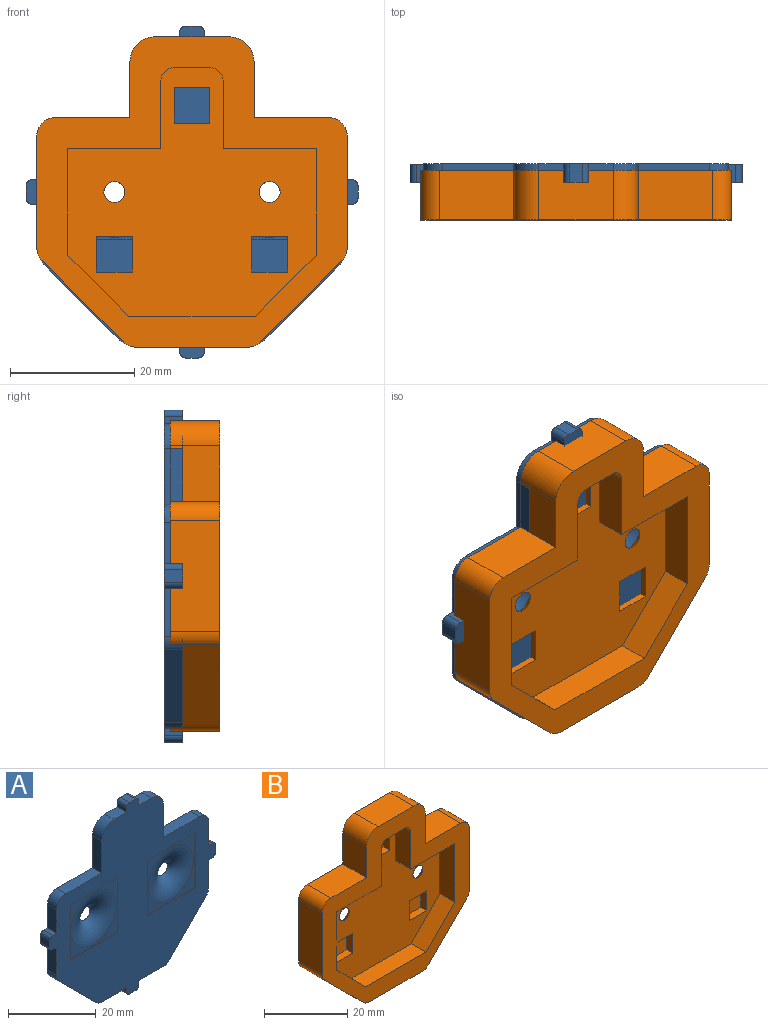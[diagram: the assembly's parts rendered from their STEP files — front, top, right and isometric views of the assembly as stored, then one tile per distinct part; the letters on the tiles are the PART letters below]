
ASSEMBLY  parts=2 mates=1
PART A: 71 faces, bbox 53.5x7.2x53.5 mm
  f0: plane 53.5x53.5mm, normal (0,-1,0), area 1397.6mm2, adj f2,f3,f4,f5,f6,f7,f8,f9
  f1: plane 53.5x53.5mm, normal (0,1,0), area 1752.8mm2, adj f2,f3,f4,f5,f6,f7,f8,f9
  f2: plane 6.55x3mm, normal (-1,0,0), area 19.7mm2, adj f0,f1,f3,f32
  f3: plane 3x1.2mm, normal (0,0,1), area 3.6mm2, adj f0,f1,f2,f69
  f4: plane 3x2mm, normal (-1,0,0), area 6mm2, adj f0,f1,f69,f70
  f5: plane 3x1.2mm, normal (0,0,-1), area 3.6mm2, adj f0,f1,f6,f70
  f6: plane 7.8x3mm, normal (-1,0,0), area 23.4mm2, adj f0,f1,f5,f30
  f7: plane 11.75x11.75mm, normal (-0.71,0,-0.71), area 49.9mm2, adj f0,f1,f30,f31
  f8: plane 7.8x3mm, normal (0,0,-1), area 23.4mm2, adj f0,f1,f9,f31
  f9: plane 3x1.2mm, normal (-1,0,0), area 3.6mm2, adj f0,f1,f8,f67
  f10: plane 3x2mm, normal (0,0,-1), area 6mm2, adj f0,f1,f67,f68
  f11: plane 3x1.2mm, normal (1,0,0), area 3.6mm2, adj f0,f1,f12,f68
  f12: plane 7.8x3mm, normal (0,0,-1), area 23.4mm2, adj f0,f1,f11,f33
  f13: plane 11.75x11.75mm, normal (0.71,0,-0.71), area 49.9mm2, adj f0,f1,f33,f34
  f14: plane 7.8x3mm, normal (1,0,0), area 23.4mm2, adj f0,f1,f15,f34
  f15: plane 3x1.2mm, normal (0,0,-1), area 3.6mm2, adj f0,f1,f14,f65
  f16: plane 3x2mm, normal (1,0,0), area 6mm2, adj f0,f1,f65,f66
  f17: plane 3x1.2mm, normal (0,0,1), area 3.6mm2, adj f0,f1,f18,f66
  f18: plane 6.55x3mm, normal (1,0,0), area 19.7mm2, adj f0,f1,f17,f35
  f19: plane 11.55x3mm, normal (0,0,1), area 34.6mm2, adj f0,f1,f20,f35
  f20: plane 9x3mm, normal (1,0,0), area 27mm2, adj f0,f1,f19,f21
  f21: cylinder r=4mm len=4mm, axis (0,1,0), area 18.8mm2, adj f0,f1,f20,f22
  f22: plane 4x3mm, normal (0,0,1), area 12mm2, adj f0,f1,f21,f23
  f23: plane 3x1.2mm, normal (1,0,0), area 3.6mm2, adj f0,f1,f22,f63
  f24: plane 3x2mm, normal (0,0,1), area 6mm2, adj f0,f1,f63,f64
  f25: plane 3x1.2mm, normal (-1,0,0), area 3.6mm2, adj f0,f1,f26,f64
  f26: plane 4x3mm, normal (0,0,1), area 12mm2, adj f0,f1,f25,f27
  f27: cylinder r=4mm len=4mm, axis (0,1,0), area 18.8mm2, adj f0,f1,f26,f28
  f28: plane 9x3mm, normal (-1,0,0), area 27mm2, adj f0,f1,f27,f29
  f29: plane 11.55x3mm, normal (0,0,1), area 34.6mm2, adj f0,f1,f28,f32
  f30: cylinder r=3mm len=3mm, axis (0,1,0), area 7.1mm2, adj f0,f1,f6,f7
  f31: cylinder r=3mm len=3mm, axis (0,1,0), area 7.1mm2, adj f0,f1,f7,f8
  f32: cylinder r=3mm len=3mm, axis (0,-1,0), area 14.1mm2, adj f0,f1,f2,f29
  f33: cylinder r=3mm len=3mm, axis (0,1,0), area 7.1mm2, adj f0,f1,f12,f13
  f34: cylinder r=3mm len=3mm, axis (0,-1,0), area 7.1mm2, adj f0,f1,f13,f14
  f35: cylinder r=3mm len=3mm, axis (0,1,0), area 14.1mm2, adj f0,f1,f18,f19
  f36: plane 5.8x2mm, normal (0,0,1), area 11.6mm2, adj f1,f37,f39,f40
  f37: plane 5.8x2mm, normal (1,0,0), area 11.6mm2, adj f1,f36,f38,f40
  f38: plane 5.8x2mm, normal (0,0,-1), area 11.6mm2, adj f1,f37,f39,f40
  f39: plane 5.8x2mm, normal (-1,0,0), area 11.6mm2, adj f1,f36,f38,f40
  f40: plane 5.8x5.8mm, normal (0,1,0), area 33.6mm2, adj f36,f37,f38,f39
  f41: plane 5.8x2mm, normal (0,0,1), area 11.6mm2, adj f1,f42,f44,f45
  f42: plane 5.8x2mm, normal (1,0,0), area 11.6mm2, adj f1,f41,f43,f45
  f43: plane 5.8x2mm, normal (0,0,-1), area 11.6mm2, adj f1,f42,f44,f45
  f44: plane 5.8x2mm, normal (-1,0,0), area 11.6mm2, adj f1,f41,f43,f45
  f45: plane 5.8x5.8mm, normal (0,1,0), area 33.6mm2, adj f41,f42,f43,f44
  f46: plane 5.8x2mm, normal (-1,0,0), area 11.6mm2, adj f1,f47,f49,f50
  f47: plane 5.8x2mm, normal (0,0,1), area 11.6mm2, adj f1,f46,f48,f50
  f48: plane 5.8x2mm, normal (1,0,0), area 11.6mm2, adj f1,f47,f49,f50
  f49: plane 5.8x2mm, normal (0,0,-1), area 11.6mm2, adj f1,f46,f48,f50
  f50: plane 5.8x5.8mm, normal (0,1,0), area 33.6mm2, adj f46,f47,f48,f49
  f51: plane 15.4x0.2mm, normal (0,0,-1), area 3.1mm2, adj f0,f52,f54,f55
  f52: plane 15.4x0.2mm, normal (1,0,0), area 3.1mm2, adj f0,f51,f53,f55
  f53: plane 15.4x0.2mm, normal (0,0,1), area 3.1mm2, adj f0,f52,f54,f55
  f54: plane 15.4x0.2mm, normal (-1,0,0), area 3.1mm2, adj f0,f51,f53,f55
  f55: plane 15.4x15.4mm, normal (0,-1,0), area 69.7mm2, adj f51,f52,f53,f54,f61
  f56: plane 15.4x0.2mm, normal (-1,0,0), area 3.1mm2, adj f0,f57,f59,f60
  f57: plane 15.4x0.2mm, normal (0,0,-1), area 3.1mm2, adj f0,f56,f58,f60
  f58: plane 15.4x0.2mm, normal (1,0,0), area 3.1mm2, adj f0,f57,f59,f60
  f59: plane 15.4x0.2mm, normal (0,0,1), area 3.1mm2, adj f0,f56,f58,f60
  f60: plane 15.4x15.4mm, normal (0,-1,0), area 69.7mm2, adj f56,f57,f58,f59,f62
  f61: torus R=7.3mm, axis (0,-1,0), area 174.6mm2, adj f1,f55
  f62: torus R=7.3mm, axis (0,-1,0), area 174.6mm2, adj f1,f60
  f63: cylinder r=1mm len=3mm, axis (0,1,0), area 4.7mm2, adj f0,f1,f23,f24
  f64: cylinder r=1mm len=3mm, axis (0,-1,0), area 4.7mm2, adj f0,f1,f24,f25
  f65: cylinder r=1mm len=3mm, axis (0,-1,0), area 4.7mm2, adj f0,f1,f15,f16
  f66: cylinder r=1mm len=3mm, axis (0,1,0), area 4.7mm2, adj f0,f1,f16,f17
  f67: cylinder r=1mm len=3mm, axis (0,1,0), area 4.7mm2, adj f0,f1,f9,f10
  f68: cylinder r=1mm len=3mm, axis (0,-1,0), area 4.7mm2, adj f0,f1,f10,f11
  f69: cylinder r=1mm len=3mm, axis (0,-1,0), area 4.7mm2, adj f0,f1,f3,f4
  f70: cylinder r=1mm len=3mm, axis (0,1,0), area 4.7mm2, adj f0,f1,f4,f5
PART B: 60 faces, bbox 50x8x50 mm
  f0: plane 40x40mm, normal (0,-1,0), area 993.2mm2, adj f14,f15,f16,f17,f18,f19,f20,f21
  f1: plane 50x50mm, normal (0,1,0), area 1405.1mm2, adj f2,f3,f4,f5,f6,f7,f8,f9
  f2: plane 17.91x8mm, normal (0,0,-1), area 143.3mm2, adj f1,f26,f39,f40
  f3: plane 13.04x13.04mm, normal (0.71,0,-0.71), area 147.6mm2, adj f1,f26,f40,f41
  f4: plane 17.96x8mm, normal (1,0,0), area 143.7mm2, adj f1,f26,f41,f42
  f5: plane 12x8mm, normal (0,0,1), area 96mm2, adj f1,f6,f26,f42
  f6: plane 9x8mm, normal (1,0,0), area 72mm2, adj f1,f5,f7,f26
  f7: cylinder r=4mm len=8mm, axis (0,1,0), area 50.3mm2, adj f1,f6,f8,f26
  f8: plane 12x8mm, normal (0,0,1), area 96mm2, adj f1,f7,f9,f26
  f9: cylinder r=4mm len=8mm, axis (0,1,0), area 50.3mm2, adj f1,f8,f10,f26
  f10: plane 9x8mm, normal (-1,0,0), area 72mm2, adj f1,f9,f11,f26
  f11: plane 12x8mm, normal (0,0,1), area 96mm2, adj f1,f10,f26,f37
  f12: plane 17.96x8mm, normal (-1,0,0), area 143.7mm2, adj f1,f26,f37,f38
  f13: plane 13.04x13.04mm, normal (-0.71,0,-0.71), area 147.6mm2, adj f1,f26,f38,f39
  f14: plane 15x5mm, normal (0,0,-1), area 75mm2, adj f0,f15,f25,f26
  f15: plane 11x5mm, normal (1,0,0), area 55mm2, adj f0,f14,f16,f26
  f16: cylinder r=2mm len=5mm, axis (0,1,0), area 15.7mm2, adj f0,f15,f17,f26
  f17: plane 6x5mm, normal (0,0,-1), area 30mm2, adj f0,f16,f18,f26
  f18: cylinder r=2mm len=5mm, axis (0,1,0), area 15.7mm2, adj f0,f17,f19,f26
  f19: plane 11x5mm, normal (-1,0,0), area 55mm2, adj f0,f18,f20,f26
  f20: plane 15x5mm, normal (0,0,-1), area 75mm2, adj f0,f19,f21,f26
  f21: plane 17.2x5mm, normal (-1,0,0), area 86mm2, adj f0,f20,f22,f26
  f22: plane 9.8x9.8mm, normal (-0.71,0,0.71), area 69.3mm2, adj f0,f21,f23,f26
  f23: plane 20.4x5mm, normal (0,0,1), area 102mm2, adj f0,f22,f24,f26
  f24: plane 9.8x9.8mm, normal (0.71,0,0.71), area 69.3mm2, adj f0,f23,f25,f26
  f25: plane 17.2x5mm, normal (1,0,0), area 86mm2, adj f0,f14,f24,f26
  f26: plane 50x50mm, normal (0,-1,0), area 767.2mm2, adj f2,f3,f4,f5,f6,f7,f8,f9
  f27: plane 15.4x0.2mm, normal (0,0,-1), area 3.1mm2, adj f1,f28,f30,f31
  f28: plane 15.4x0.2mm, normal (-1,0,0), area 3.1mm2, adj f1,f27,f29,f31
  f29: plane 15.4x0.2mm, normal (0,0,1), area 3.1mm2, adj f1,f28,f30,f31
  f30: plane 15.4x0.2mm, normal (1,0,0), area 3.1mm2, adj f1,f27,f29,f31
  f31: plane 15.4x15.4mm, normal (0,1,0), area 69.7mm2, adj f27,f28,f29,f30,f58
  f32: plane 15.4x0.2mm, normal (1,0,0), area 3.1mm2, adj f1,f33,f35,f36
  f33: plane 15.4x0.2mm, normal (0,0,-1), area 3.1mm2, adj f1,f32,f34,f36
  f34: plane 15.4x0.2mm, normal (-1,0,0), area 3.1mm2, adj f1,f33,f35,f36
  f35: plane 15.4x0.2mm, normal (0,0,1), area 3.1mm2, adj f1,f32,f34,f36
  f36: plane 15.4x15.4mm, normal (0,1,0), area 69.7mm2, adj f32,f33,f34,f35,f59
  f37: cylinder r=3mm len=8mm, axis (0,-1,0), area 37.7mm2, adj f1,f11,f12,f26
  f38: cylinder r=3mm len=8mm, axis (0,1,0), area 18.8mm2, adj f1,f12,f13,f26
  f39: cylinder r=3mm len=8mm, axis (0,1,0), area 18.8mm2, adj f1,f2,f13,f26
  f40: cylinder r=3mm len=8mm, axis (0,1,0), area 18.8mm2, adj f1,f2,f3,f26
  f41: cylinder r=3mm len=8mm, axis (0,-1,0), area 18.8mm2, adj f1,f3,f4,f26
  f42: cylinder r=3mm len=8mm, axis (0,1,0), area 37.7mm2, adj f1,f4,f5,f26
  f43: plane 5.8x2mm, normal (0,0,-1), area 11.6mm2, adj f0,f44,f46,f47
  f44: plane 5.8x2mm, normal (1,0,0), area 11.6mm2, adj f0,f43,f45,f47
  f45: plane 5.8x2mm, normal (0,0,1), area 11.6mm2, adj f0,f44,f46,f47
  f46: plane 5.8x2mm, normal (-1,0,0), area 11.6mm2, adj f0,f43,f45,f47
  f47: plane 5.8x5.8mm, normal (0,-1,0), area 33.6mm2, adj f43,f44,f45,f46
  f48: plane 5.8x2mm, normal (0,0,1), area 11.6mm2, adj f0,f49,f51,f52
  f49: plane 5.8x2mm, normal (-1,0,0), area 11.6mm2, adj f0,f48,f50,f52
  f50: plane 5.8x2mm, normal (0,0,-1), area 11.6mm2, adj f0,f49,f51,f52
  f51: plane 5.8x2mm, normal (1,0,0), area 11.6mm2, adj f0,f48,f50,f52
  f52: plane 5.8x5.8mm, normal (0,-1,0), area 33.6mm2, adj f48,f49,f50,f51
  f53: plane 5.8x2mm, normal (0,0,-1), area 11.6mm2, adj f0,f54,f56,f57
  f54: plane 5.8x2mm, normal (1,0,0), area 11.6mm2, adj f0,f53,f55,f57
  f55: plane 5.8x2mm, normal (0,0,1), area 11.6mm2, adj f0,f54,f56,f57
  f56: plane 5.8x2mm, normal (-1,0,0), area 11.6mm2, adj f0,f53,f55,f57
  f57: plane 5.8x5.8mm, normal (0,-1,0), area 33.6mm2, adj f53,f54,f55,f56
  f58: torus R=7.3mm, axis (0,1,0), area 174.6mm2, adj f0,f31
  f59: torus R=7.3mm, axis (0,1,0), area 174.6mm2, adj f0,f36
PLACE A t=(-30.62,-1.03,-29.8)mm
PLACE B t=(-21.74,-2.03,-73.31)mm
MATE fastened B.f57 <-> A.f50  axis (0,-1,0) through (-28.62,-3.03,-8.78)mm
